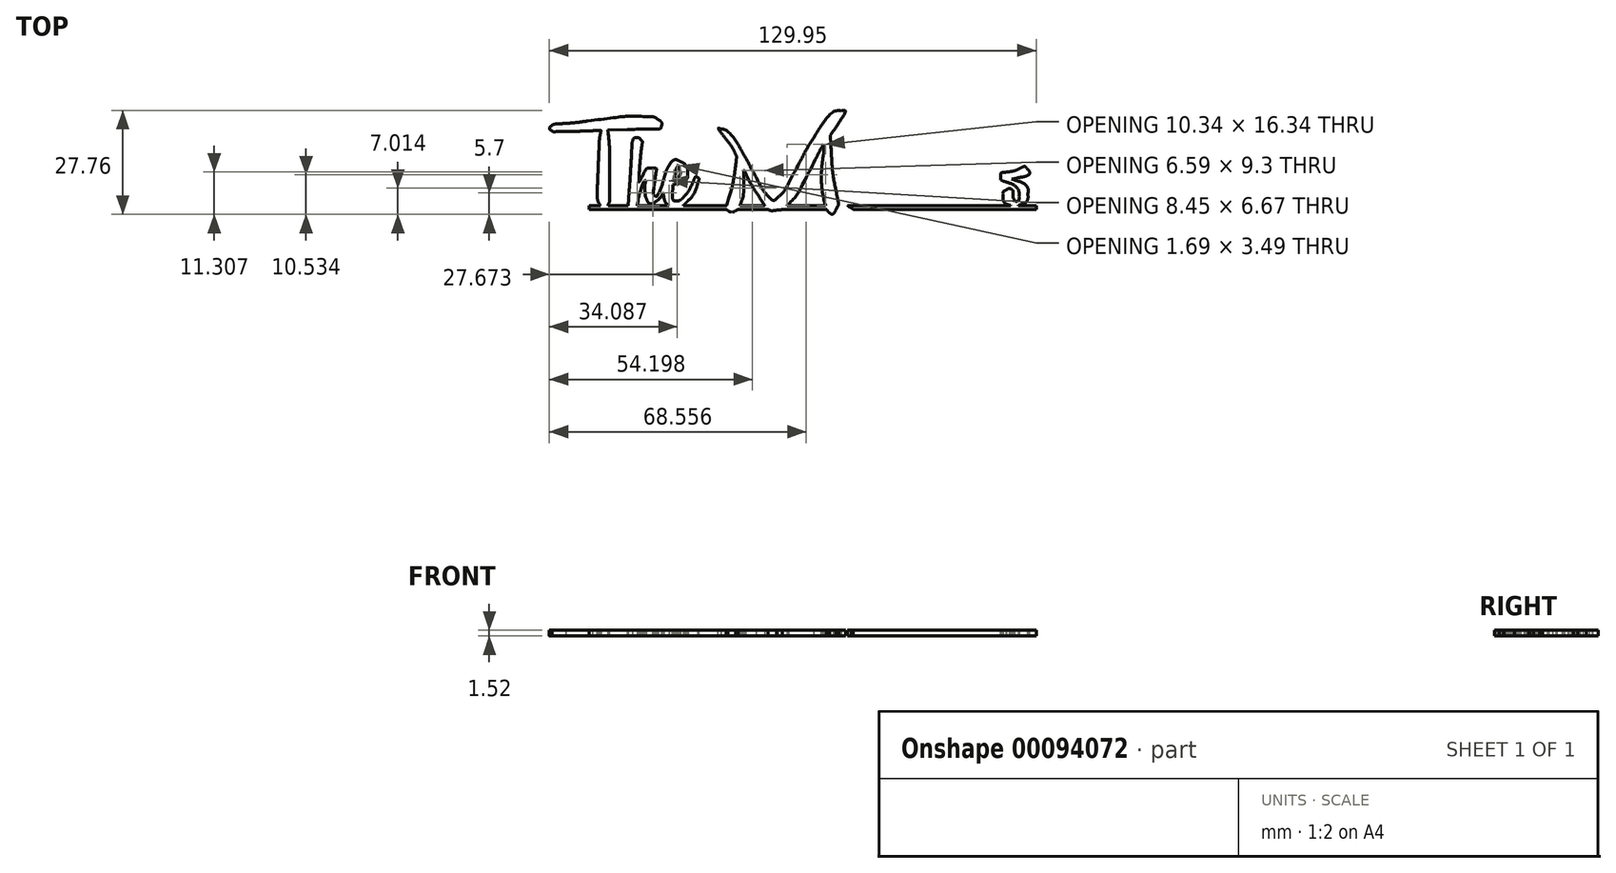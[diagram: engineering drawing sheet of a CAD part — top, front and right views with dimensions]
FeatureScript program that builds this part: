
annotation { "Feature Type Name" : "Feature", "Feature Type Description" : "" }
export const myFeature = defineFeature(function(context is Context, id is Id, definition is map)
    precondition{}
    {
        {
            var Q0;
            Q0=qCreatedBy(makeId("Top.planeOp"),FACE);
            var sketch = newSketch(context, id + "F0", { "sketchPlane" : qUnion([Q0])});
            skLineSegment(sketch, "E0", {"start": v(8.55, 2.32) * mm, "end": v(8.5, 2.84) * mm});
            skLineSegment(sketch, "E1", {"start": v(8.5, 2.84) * mm, "end": v(8.07, 2.18) * mm});
            skLineSegment(sketch, "E2", {"start": v(8.07, 2.18) * mm, "end": v(8.55, 2.32) * mm});
            skLineSegment(sketch, "E3", {"start": v(11.05, 6.37) * mm, "end": v(10.27, 5.29) * mm});
            skLineSegment(sketch, "E4", {"start": v(10.27, 5.29) * mm, "end": v(10.4, 2.62) * mm});
            skLineSegment(sketch, "E5", {"start": v(10.4, 2.62) * mm, "end": v(11.05, 6.37) * mm});
            skLineSegment(sketch, "E6", {"start": v(-44.03, 6.78) * mm, "end": v(-49.15, 6.7) * mm});
            skLineSegment(sketch, "E7", {"start": v(-49.15, 6.7) * mm, "end": v(-49.07, 5.94) * mm});
            skLineSegment(sketch, "E8", {"start": v(-49.07, 5.94) * mm, "end": v(-44.03, 6.78) * mm});
            skLineSegment(sketch, "E9", {"start": v(26.41, -4.76) * mm, "end": v(26.32, -5.42) * mm});
            skLineSegment(sketch, "E10", {"start": v(26.32, -5.42) * mm, "end": v(27.3, -5.33) * mm});
            skLineSegment(sketch, "E11", {"start": v(27.3, -5.33) * mm, "end": v(26.41, -4.76) * mm});
            skLineSegment(sketch, "E12", {"start": v(28.58, -5.48) * mm, "end": v(28.88, -5.73) * mm});
            skLineSegment(sketch, "E13", {"start": v(28.88, -5.73) * mm, "end": v(28.67, -6.78) * mm});
            skLineSegment(sketch, "E14", {"start": v(28.67, -6.78) * mm, "end": v(28.58, -5.48) * mm});
            skLineSegment(sketch, "E15", {"start": v(30.62, -0.91) * mm, "end": v(31.32, -0.91) * mm});
            skLineSegment(sketch, "E16", {"start": v(31.32, -0.91) * mm, "end": v(31.39, -0.12) * mm});
            skLineSegment(sketch, "E17", {"start": v(31.39, -0.12) * mm, "end": v(30.62, -0.91) * mm});
            skLineSegment(sketch, "E18", {"start": v(34.08, 0) * mm, "end": v(34.01, -0.78) * mm});
            skLineSegment(sketch, "E19", {"start": v(34.01, -0.78) * mm, "end": v(34.72, -0.78) * mm});
            skLineSegment(sketch, "E20", {"start": v(34.72, -0.78) * mm, "end": v(34.08, 0) * mm});
            skLineSegment(sketch, "E21", {"start": v(33.6, -11.13) * mm, "end": v(33.73, -11.48) * mm});
            skLineSegment(sketch, "E22", {"start": v(33.73, -11.48) * mm, "end": v(34.04, -11.2) * mm});
            skLineSegment(sketch, "E23", {"start": v(34.04, -11.2) * mm, "end": v(33.6, -11.13) * mm});
            skLineSegment(sketch, "E24", {"start": v(43.61, -8.09) * mm, "end": v(43.62, -8.61) * mm});
            skLineSegment(sketch, "E25", {"start": v(43.62, -8.61) * mm, "end": v(43.8, -8.15) * mm});
            skLineSegment(sketch, "E26", {"start": v(43.8, -8.15) * mm, "end": v(43.61, -8.09) * mm});
            skLineSegment(sketch, "E27", {"start": v(45.2, -8.8) * mm, "end": v(45.1, -7.82) * mm});
            skLineSegment(sketch, "E28", {"start": v(45.1, -7.82) * mm, "end": v(44.76, -8.55) * mm});
            skLineSegment(sketch, "E29", {"start": v(44.76, -8.55) * mm, "end": v(45.2, -8.8) * mm});
            skLineSegment(sketch, "E30", {"start": v(41.23, -11.08) * mm, "end": v(41.23, -10.34) * mm});
            skLineSegment(sketch, "E31", {"start": v(41.23, -10.34) * mm, "end": v(40.72, -11.2) * mm});
            skLineSegment(sketch, "E32", {"start": v(40.72, -11.2) * mm, "end": v(41.23, -11.08) * mm});
            skLineSegment(sketch, "E33", {"start": v(36.47, -11.02) * mm, "end": v(36.31, -10.52) * mm});
            skLineSegment(sketch, "E34", {"start": v(36.31, -10.52) * mm, "end": v(35.94, -11.2) * mm});
            skLineSegment(sketch, "E35", {"start": v(35.94, -11.2) * mm, "end": v(36.47, -11.02) * mm});
            skLineSegment(sketch, "E36", {"start": v(31.17, -11.28) * mm, "end": v(31, -10.46) * mm});
            skLineSegment(sketch, "E37", {"start": v(31, -10.46) * mm, "end": v(30.7, -11.04) * mm});
            skLineSegment(sketch, "E38", {"start": v(30.7, -11.04) * mm, "end": v(31.17, -11.28) * mm});
            skLineSegment(sketch, "E39", {"start": v(20.22, -12.06) * mm, "end": v(19.85, -11.6) * mm});
            skLineSegment(sketch, "E40", {"start": v(19.85, -11.6) * mm, "end": v(19.56, -12.22) * mm});
            skLineSegment(sketch, "E41", {"start": v(19.56, -12.22) * mm, "end": v(20.22, -12.06) * mm});
            skLineSegment(sketch, "E42", {"start": v(17.89, -12.47) * mm, "end": v(17.89, -12.47) * mm});
            skLineSegment(sketch, "E43", {"start": v(-43.45, -13.85) * mm, "end": v(-43.74, -13.61) * mm});
            skLineSegment(sketch, "E44", {"start": v(-43.74, -13.61) * mm, "end": v(-43.47, -9.8) * mm});
            skLineSegment(sketch, "E45", {"start": v(-43.47, -9.8) * mm, "end": v(-43.45, -13.85) * mm});
            skLineSegment(sketch, "E46", {"start": v(-30.74, -7.76) * mm, "end": v(-31.8, -7.97) * mm});
            skLineSegment(sketch, "E47", {"start": v(-31.8, -7.97) * mm, "end": v(-31.83, -9.31) * mm});
            skLineSegment(sketch, "E48", {"start": v(-31.83, -9.31) * mm, "end": v(-30.74, -7.76) * mm});
            skLineSegment(sketch, "E49", {"start": v(59.14, -6.38) * mm, "end": v(58.68, -6.48) * mm});
            skLineSegment(sketch, "E50", {"start": v(58.68, -6.48) * mm, "end": v(59.34, -6.7) * mm});
            skLineSegment(sketch, "E51", {"start": v(59.34, -6.7) * mm, "end": v(59.14, -6.38) * mm});
            skFitSpline(sketch, "E52", {"points": [v(10.05, -15.46) * mm, v(9.66, -15.18) * mm, v(9.18, -14.22) * mm, v(8.91, -13.16) * mm]});
            skFitSpline(sketch, "E53", {"points": [v(8.91, -13.16) * mm, v(8.15, -10.15) * mm, v(7.9, -4.36) * mm, v(8.35, -0.32) * mm]});
            skFitSpline(sketch, "E54", {"points": [v(8.35, -0.32) * mm, v(8.48, 0.84) * mm, v(8.57, 2.03) * mm, v(8.55, 2.32) * mm]});
            skFitSpline(sketch, "E55", {"points": [v(8.07, 2.18) * mm, v(7.84, 1.82) * mm, v(7.2, 0.64) * mm, v(6.64, -0.45) * mm]});
            skFitSpline(sketch, "E56", {"points": [v(6.64, -0.45) * mm, v(2.6, -8.4) * mm, v(0.9, -11.22) * mm, v(-0.92, -13.04) * mm]});
            skFitSpline(sketch, "E57", {"points": [v(-0.92, -13.04) * mm, v(-2.11, -14.22) * mm, v(-2.9, -14.64) * mm, v(-4.04, -14.72) * mm]});
            skFitSpline(sketch, "E58", {"points": [v(-4.04, -14.72) * mm, v(-5.8, -14.83) * mm, v(-7.07, -13.74) * mm, v(-9.5, -10) * mm]});
            skFitSpline(sketch, "E59", {"points": [v(-9.5, -10) * mm, v(-10.49, -8.48) * mm, v(-11.77, -6.2) * mm, v(-12.36, -4.9) * mm]});
            skFitSpline(sketch, "E60", {"points": [v(-12.36, -4.9) * mm, v(-12.54, -4.51) * mm, v(-12.73, -4.2) * mm, v(-12.79, -4.2) * mm]});
            skFitSpline(sketch, "E61", {"points": [v(-12.79, -4.2) * mm, v(-12.85, -4.2) * mm, v(-12.9, -5.31) * mm, v(-12.9, -6.67) * mm]});
            skFitSpline(sketch, "E62", {"points": [v(-12.9, -6.67) * mm, v(-12.9, -9.72) * mm, v(-13.06, -11.2) * mm, v(-13.55, -12.6) * mm]});
            skFitSpline(sketch, "E63", {"points": [v(-13.55, -12.6) * mm, v(-14, -13.93) * mm, v(-14.38, -14.5) * mm, v(-15.05, -14.88) * mm]});
            skFitSpline(sketch, "E64", {"points": [v(-15.05, -14.88) * mm, v(-15.65, -15.21) * mm, v(-16.6, -15.17) * mm, v(-17.19, -14.79) * mm]});
            skFitSpline(sketch, "E65", {"points": [v(-17.19, -14.79) * mm, v(-17.51, -14.57) * mm, v(-17.53, -14.51) * mm, v(-17.46, -13.86) * mm]});
            skFitSpline(sketch, "E66", {"points": [v(-17.46, -13.86) * mm, v(-17.41, -13.48) * mm, v(-17.16, -12.47) * mm, v(-16.9, -11.62) * mm]});
            skFitSpline(sketch, "E67", {"points": [v(-16.9, -11.62) * mm, v(-16.08, -8.9) * mm, v(-15.43, -5.59) * mm, v(-14.9, -1.44) * mm]});
            skFitSpline(sketch, "E68", {"points": [v(-14.9, -1.44) * mm, v(-14.77, -0.47) * mm, v(-14.78, -0.43) * mm, v(-15.2, 0.5) * mm]});
            skFitSpline(sketch, "E69", {"points": [v(-15.2, 0.5) * mm, v(-15.7, 1.58) * mm, v(-16.3, 2.49) * mm, v(-17.9, 4.62) * mm]});
            skFitSpline(sketch, "E70", {"points": [v(-17.9, 4.62) * mm, v(-19.5, 6.73) * mm, v(-19.66, 7.1) * mm, v(-18.99, 6.93) * mm]});
            skFitSpline(sketch, "E71", {"points": [v(-18.99, 6.93) * mm, v(-17.63, 6.6) * mm, v(-15.05, 3.84) * mm, v(-13.26, 0.78) * mm]});
            skFitSpline(sketch, "E72", {"points": [v(-13.26, 0.78) * mm, v(-12.86, 0.1) * mm, v(-11.8, -1.81) * mm, v(-10.93, -3.47) * mm]});
            skFitSpline(sketch, "E73", {"points": [v(-10.93, -3.47) * mm, v(-8.28, -8.46) * mm, v(-7.49, -9.76) * mm, v(-6.46, -10.83) * mm]});
            skFitSpline(sketch, "E74", {"points": [v(-6.46, -10.83) * mm, v(-5.31, -12.03) * mm, v(-4.66, -12.14) * mm, v(-3.74, -11.3) * mm]});
            skFitSpline(sketch, "E75", {"points": [v(-3.74, -11.3) * mm, v(-2.47, -10.12) * mm, v(-1.25, -8.2) * mm, v(1.55, -2.9) * mm]});
            skFitSpline(sketch, "E76", {"points": [v(1.55, -2.9) * mm, v(3.65, 1.06) * mm, v(4.61, 2.76) * mm, v(5.77, 4.55) * mm]});
            skFitSpline(sketch, "E77", {"points": [v(5.77, 4.55) * mm, v(8.66, 9) * mm, v(11.34, 11.64) * mm, v(13.12, 11.76) * mm]});
            skFitSpline(sketch, "E78", {"points": [v(13.12, 11.76) * mm, v(14.2, 11.83) * mm, v(14.08, 11.11) * mm, v(12.57, 8.66) * mm]});
            skFitSpline(sketch, "E79", {"points": [v(12.57, 8.66) * mm, v(12.16, 8) * mm, v(11.47, 6.96) * mm, v(11.05, 6.37) * mm]});
            skFitSpline(sketch, "E80", {"points": [v(10.4, 2.62) * mm, v(10.68, -2.42) * mm, v(11.06, -6.05) * mm, v(11.6, -8.81) * mm]});
            skFitSpline(sketch, "E81", {"points": [v(11.6, -8.81) * mm, v(12.35, -12.63) * mm, v(12.38, -13.33) * mm, v(11.8, -14.47) * mm]});
            skFitSpline(sketch, "E82", {"points": [v(11.8, -14.47) * mm, v(11.28, -15.49) * mm, v(10.62, -15.86) * mm, v(10.05, -15.46) * mm]});
            skFitSpline(sketch, "E83", {"points": [v(-50.1, -14.15) * mm, v(-50.65, -13.91) * mm, v(-51.56, -12.92) * mm, v(-51.73, -12.37) * mm]});
            skFitSpline(sketch, "E84", {"points": [v(-51.73, -12.37) * mm, v(-51.95, -11.68) * mm, v(-51.97, -9.22) * mm, v(-51.78, -4.66) * mm]});
            skFitSpline(sketch, "E85", {"points": [v(-51.78, -4.66) * mm, v(-51.49, 2.35) * mm, v(-51.36, 4.44) * mm, v(-51.16, 5.5) * mm]});
            skFitSpline(sketch, "E86", {"points": [v(-51.16, 5.5) * mm, v(-51.05, 6.05) * mm, v(-50.98, 6.52) * mm, v(-51, 6.53) * mm]});
            skFitSpline(sketch, "E87", {"points": [v(-51, 6.53) * mm, v(-51.01, 6.54) * mm, v(-52.03, 6.5) * mm, v(-53.26, 6.45) * mm]});
            skFitSpline(sketch, "E88", {"points": [v(-53.26, 6.45) * mm, v(-54.5, 6.4) * mm, v(-57.34, 6.31) * mm, v(-59.58, 6.26) * mm]});
            skFitSpline(sketch, "E89", {"points": [v(-59.58, 6.26) * mm, v(-63.56, 6.18) * mm, v(-63.68, 6.19) * mm, v(-64.1, 6.45) * mm]});
            skFitSpline(sketch, "E90", {"points": [v(-64.1, 6.45) * mm, v(-64.65, 6.8) * mm, v(-64.68, 7.37) * mm, v(-64.19, 7.76) * mm]});
            skFitSpline(sketch, "E91", {"points": [v(-64.19, 7.76) * mm, v(-63.74, 8.11) * mm, v(-62.93, 8.25) * mm, v(-60.3, 8.42) * mm]});
            skFitSpline(sketch, "E92", {"points": [v(-60.3, 8.42) * mm, v(-59.11, 8.5) * mm, v(-56.5, 8.77) * mm, v(-54.51, 9.03) * mm]});
            skFitSpline(sketch, "E93", {"points": [v(-54.51, 9.03) * mm, v(-46.34, 10.09) * mm, v(-43.17, 10.35) * mm, v(-39.68, 10.25) * mm]});
            skFitSpline(sketch, "E94", {"points": [v(-39.68, 10.25) * mm, v(-37.3, 10.19) * mm, v(-36.64, 10.05) * mm, v(-35.67, 9.4) * mm]});
            skFitSpline(sketch, "E95", {"points": [v(-35.67, 9.4) * mm, v(-35.05, 9) * mm, v(-34.68, 8.27) * mm, v(-34.84, 7.8) * mm]});
            skFitSpline(sketch, "E96", {"points": [v(-34.84, 7.8) * mm, v(-35.1, 7.06) * mm, v(-36.56, 6.9) * mm, v(-44.03, 6.78) * mm]});
            skFitSpline(sketch, "E97", {"points": [v(-49.07, 5.94) * mm, v(-48.78, 3.12) * mm, v(-48.66, 0.18) * mm, v(-48.66, -5) * mm]});
            skFitSpline(sketch, "E98", {"points": [v(-48.66, -5) * mm, v(-48.65, -11) * mm, v(-48.75, -12.57) * mm, v(-49.2, -13.69) * mm]});
            skFitSpline(sketch, "E99", {"points": [v(-49.2, -13.69) * mm, v(-49.44, -14.3) * mm, v(-49.6, -14.37) * mm, v(-50.1, -14.15) * mm]});
            skFitSpline(sketch, "E100", {"points": [v(15.79, -14.07) * mm, v(14.9, -13.6) * mm, v(14.27, -12.5) * mm, v(13.9, -10.73) * mm]});
            skFitSpline(sketch, "E101", {"points": [v(13.9, -10.73) * mm, v(13.65, -9.5) * mm, v(13.65, -8.88) * mm, v(13.9, -7.43) * mm]});
            skFitSpline(sketch, "E102", {"points": [v(13.9, -7.43) * mm, v(14.27, -5.37) * mm, v(15.27, -3.7) * mm, v(16.5, -3.11) * mm]});
            skFitSpline(sketch, "E103", {"points": [v(16.5, -3.11) * mm, v(17.07, -2.84) * mm, v(18.16, -2.82) * mm, v(18.76, -3.07) * mm]});
            skFitSpline(sketch, "E104", {"points": [v(18.76, -3.07) * mm, v(19, -3.17) * mm, v(19.37, -3.46) * mm, v(19.57, -3.71) * mm]});
            skFitSpline(sketch, "E105", {"points": [v(19.57, -3.71) * mm, v(19.92, -4.15) * mm, v(19.95, -4.16) * mm, v(20.28, -3.97) * mm]});
            skFitSpline(sketch, "E106", {"points": [v(20.28, -3.97) * mm, v(20.74, -3.7) * mm, v(21.53, -3.85) * mm, v(21.95, -4.27) * mm]});
            skFitSpline(sketch, "E107", {"points": [v(21.95, -4.27) * mm, v(22.3, -4.62) * mm, v(22.36, -5.33) * mm, v(22.14, -6.44) * mm]});
            skFitSpline(sketch, "E108", {"points": [v(22.14, -6.44) * mm, v(22.07, -6.77) * mm, v(21.98, -7.69) * mm, v(21.93, -8.48) * mm]});
            skFitSpline(sketch, "E109", {"points": [v(21.93, -8.48) * mm, v(21.83, -10.14) * mm, v(22, -11.1) * mm, v(22.37, -11.03) * mm]});
            skFitSpline(sketch, "E110", {"points": [v(22.37, -11.03) * mm, v(22.7, -10.96) * mm, v(23.38, -9.6) * mm, v(23.99, -7.74) * mm]});
            skFitSpline(sketch, "E111", {"points": [v(23.99, -7.74) * mm, v(24.42, -6.4) * mm, v(24.5, -6.02) * mm, v(24.39, -5.8) * mm]});
            skFitSpline(sketch, "E112", {"points": [v(24.39, -5.8) * mm, v(24.3, -5.66) * mm, v(24.24, -5.3) * mm, v(24.24, -4.99) * mm]});
            skFitSpline(sketch, "E113", {"points": [v(24.24, -4.99) * mm, v(24.24, -4.54) * mm, v(24.32, -4.36) * mm, v(24.69, -4) * mm]});
            skFitSpline(sketch, "E114", {"points": [v(24.69, -4) * mm, v(25.05, -3.63) * mm, v(25.24, -3.54) * mm, v(25.67, -3.54) * mm]});
            skFitSpline(sketch, "E115", {"points": [v(25.67, -3.54) * mm, v(26.36, -3.54) * mm, v(26.54, -3.84) * mm, v(26.41, -4.76) * mm]});
            skFitSpline(sketch, "E116", {"points": [v(27.3, -5.33) * mm, v(28.14, -5.25) * mm, v(28.31, -5.27) * mm, v(28.58, -5.48) * mm]});
            skFitSpline(sketch, "E117", {"points": [v(28.67, -6.78) * mm, v(28.05, -9.98) * mm, v(28.04, -11.58) * mm, v(28.65, -11.58) * mm]});
            skFitSpline(sketch, "E118", {"points": [v(28.65, -11.58) * mm, v(28.93, -11.58) * mm, v(29.43, -10.65) * mm, v(30.19, -8.75) * mm]});
            skFitSpline(sketch, "E119", {"points": [v(30.19, -8.75) * mm, v(30.83, -7.12) * mm, v(30.87, -6.93) * mm, v(31.04, -5.06) * mm]});
            skFitSpline(sketch, "E120", {"points": [v(31.04, -5.06) * mm, v(31.3, -2.01) * mm, v(31.34, -2.23) * mm, v(30.57, -2.23) * mm]});
            skFitSpline(sketch, "E121", {"points": [v(30.57, -2.23) * mm, v(29.55, -2.23) * mm, v(29, -1.88) * mm, v(29.2, -1.36) * mm]});
            skFitSpline(sketch, "E122", {"points": [v(29.2, -1.36) * mm, v(29.31, -1.07) * mm, v(29.8, -0.91) * mm, v(30.62, -0.91) * mm]});
            skFitSpline(sketch, "E123", {"points": [v(31.39, -0.12) * mm, v(31.43, 0.32) * mm, v(31.55, 0.82) * mm, v(31.67, 1) * mm]});
            skFitSpline(sketch, "E124", {"points": [v(31.67, 1) * mm, v(31.96, 1.45) * mm, v(32.8, 1.65) * mm, v(33.36, 1.42) * mm]});
            skFitSpline(sketch, "E125", {"points": [v(33.36, 1.42) * mm, v(34.05, 1.13) * mm, v(34.16, 0.9) * mm, v(34.08, 0) * mm]});
            skFitSpline(sketch, "E126", {"points": [v(34.72, -0.78) * mm, v(35.4, -0.78) * mm, v(35.44, -0.76) * mm, v(35.62, -0.34) * mm]});
            skFitSpline(sketch, "E127", {"points": [v(35.62, -0.34) * mm, v(36.27, 1.24) * mm, v(39.63, 1.57) * mm, v(40.38, 0.14) * mm]});
            skFitSpline(sketch, "E128", {"points": [v(40.38, 0.14) * mm, v(41.17, -1.39) * mm, v(38.77, -2.85) * mm, v(36.6, -2.17) * mm]});
            skFitSpline(sketch, "E129", {"points": [v(36.6, -2.17) * mm, v(36.05, -2) * mm, v(35.8, -1.98) * mm, v(35.52, -2.09) * mm]});
            skFitSpline(sketch, "E130", {"points": [v(35.52, -2.09) * mm, v(35.32, -2.16) * mm, v(34.87, -2.23) * mm, v(34.51, -2.23) * mm]});
            skFitSpline(sketch, "E131", {"points": [v(34.51, -2.23) * mm, v(33.89, -2.23) * mm, v(33.86, -2.24) * mm, v(33.8, -2.66) * mm]});
            skFitSpline(sketch, "E132", {"points": [v(33.8, -2.66) * mm, v(33.49, -4.52) * mm, v(33.35, -10.47) * mm, v(33.6, -11.13) * mm]});
            skFitSpline(sketch, "E133", {"points": [v(34.04, -11.2) * mm, v(34.39, -10.87) * mm, v(35.33, -9.03) * mm, v(35.95, -7.47) * mm]});
            skFitSpline(sketch, "E134", {"points": [v(35.95, -7.47) * mm, v(36.24, -6.77) * mm, v(36.36, -6.24) * mm, v(36.36, -5.72) * mm]});
            skFitSpline(sketch, "E135", {"points": [v(36.36, -5.72) * mm, v(36.36, -4.24) * mm, v(37.02, -3.56) * mm, v(38.1, -3.95) * mm]});
            skFitSpline(sketch, "E136", {"points": [v(38.1, -3.95) * mm, v(38.4, -4.05) * mm, v(38.75, -4.3) * mm, v(38.9, -4.48) * mm]});
            skFitSpline(sketch, "E137", {"points": [v(38.9, -4.48) * mm, v(39.14, -4.82) * mm, v(39.14, -4.86) * mm, v(38.93, -6.13) * mm]});
            skFitSpline(sketch, "E138", {"points": [v(38.93, -6.13) * mm, v(38.69, -7.53) * mm, v(38.6, -10.1) * mm, v(38.77, -10.7) * mm]});
            skFitSpline(sketch, "E139", {"points": [v(38.77, -10.7) * mm, v(38.9, -11.18) * mm, v(39.22, -11.12) * mm, v(39.6, -10.56) * mm]});
            skFitSpline(sketch, "E140", {"points": [v(39.6, -10.56) * mm, v(40.16, -9.72) * mm, v(40.98, -7.2) * mm, v(41.16, -5.73) * mm]});
            skFitSpline(sketch, "E141", {"points": [v(41.16, -5.73) * mm, v(41.26, -4.93) * mm, v(41.42, -4.2) * mm, v(41.54, -4) * mm]});
            skFitSpline(sketch, "E142", {"points": [v(41.54, -4) * mm, v(41.95, -3.4) * mm, v(42.93, -3.1) * mm, v(43.73, -3.34) * mm]});
            skFitSpline(sketch, "E143", {"points": [v(43.73, -3.34) * mm, v(44.22, -3.5) * mm, v(44.25, -3.9) * mm, v(43.92, -5.78) * mm]});
            skFitSpline(sketch, "E144", {"points": [v(43.92, -5.78) * mm, v(43.75, -6.76) * mm, v(43.61, -7.8) * mm, v(43.61, -8.09) * mm]});
            skFitSpline(sketch, "E145", {"points": [v(43.8, -8.15) * mm, v(44.06, -7.42) * mm, v(44.65, -6.29) * mm, v(45.02, -5.8) * mm]});
            skFitSpline(sketch, "E146", {"points": [v(45.02, -5.8) * mm, v(45.6, -5.03) * mm, v(46.93, -4.73) * mm, v(47.55, -5.23) * mm]});
            skFitSpline(sketch, "E147", {"points": [v(47.55, -5.23) * mm, v(47.82, -5.45) * mm, v(47.83, -5.5) * mm, v(47.67, -6.05) * mm]});
            skFitSpline(sketch, "E148", {"points": [v(47.67, -6.05) * mm, v(47.46, -6.78) * mm, v(47.43, -9.8) * mm, v(47.63, -10) * mm]});
            skFitSpline(sketch, "E149", {"points": [v(47.63, -10) * mm, v(48, -10.37) * mm, v(48.82, -9.38) * mm, v(49.86, -7.3) * mm]});
            skFitSpline(sketch, "E150", {"points": [v(49.86, -7.3) * mm, v(50.52, -5.97) * mm, v(50.78, -5.72) * mm, v(51.18, -6.05) * mm]});
            skFitSpline(sketch, "E151", {"points": [v(51.18, -6.05) * mm, v(51.54, -6.35) * mm, v(51.4, -7.04) * mm, v(50.65, -8.51) * mm]});
            skFitSpline(sketch, "E152", {"points": [v(50.65, -8.51) * mm, v(49.8, -10.21) * mm, v(48.62, -11.62) * mm, v(47.83, -11.85) * mm]});
            skFitSpline(sketch, "E153", {"points": [v(47.83, -11.85) * mm, v(47.06, -12.08) * mm, v(46.32, -11.82) * mm, v(45.84, -11.16) * mm]});
            skFitSpline(sketch, "E154", {"points": [v(45.84, -11.16) * mm, v(45.42, -10.59) * mm, v(45.34, -10.29) * mm, v(45.2, -8.8) * mm]});
            skFitSpline(sketch, "E155", {"points": [v(44.76, -8.55) * mm, v(44.58, -8.95) * mm, v(44.33, -9.72) * mm, v(44.2, -10.26) * mm]});
            skFitSpline(sketch, "E156", {"points": [v(44.2, -10.26) * mm, v(43.78, -12.15) * mm, v(43.76, -12.2) * mm, v(43.28, -12.42) * mm]});
            skFitSpline(sketch, "E157", {"points": [v(43.28, -12.42) * mm, v(42.73, -12.68) * mm, v(42.25, -12.69) * mm, v(41.77, -12.44) * mm]});
            skFitSpline(sketch, "E158", {"points": [v(41.77, -12.44) * mm, v(41.3, -12.2) * mm, v(41.23, -12.01) * mm, v(41.23, -11.08) * mm]});
            skFitSpline(sketch, "E159", {"points": [v(40.72, -11.2) * mm, v(40.1, -12.23) * mm, v(39.29, -12.9) * mm, v(38.65, -12.9) * mm]});
            skFitSpline(sketch, "E160", {"points": [v(38.65, -12.9) * mm, v(37.65, -12.9) * mm, v(36.82, -12.18) * mm, v(36.47, -11.02) * mm]});
            skFitSpline(sketch, "E161", {"points": [v(35.94, -11.2) * mm, v(35.1, -12.72) * mm, v(34.12, -13.55) * mm, v(33.13, -13.55) * mm]});
            skFitSpline(sketch, "E162", {"points": [v(33.13, -13.55) * mm, v(32.11, -13.55) * mm, v(31.48, -12.82) * mm, v(31.17, -11.28) * mm]});
            skFitSpline(sketch, "E163", {"points": [v(30.7, -11.04) * mm, v(30.31, -11.8) * mm, v(29.3, -12.89) * mm, v(28.76, -13.11) * mm]});
            skFitSpline(sketch, "E164", {"points": [v(28.76, -13.11) * mm, v(28.12, -13.38) * mm, v(27.24, -13.34) * mm, v(26.84, -13.02) * mm]});
            skFitSpline(sketch, "E165", {"points": [v(26.84, -13.02) * mm, v(26.65, -12.88) * mm, v(26.37, -12.42) * mm, v(26.2, -12) * mm]});
            skFitSpline(sketch, "E166", {"points": [v(26.2, -12) * mm, v(25.84, -11.05) * mm, v(25.8, -8.95) * mm, v(26.13, -7.59) * mm]});
            skFitSpline(sketch, "E167", {"points": [v(26.13, -7.59) * mm, v(26.4, -6.45) * mm, v(26.4, -6.47) * mm, v(26.04, -6.54) * mm]});
            skFitSpline(sketch, "E168", {"points": [v(26.04, -6.54) * mm, v(25.77, -6.59) * mm, v(25.68, -6.76) * mm, v(25.43, -7.6) * mm]});
            skFitSpline(sketch, "E169", {"points": [v(25.43, -7.6) * mm, v(24.7, -10.16) * mm, v(23.79, -11.88) * mm, v(22.84, -12.53) * mm]});
            skFitSpline(sketch, "E170", {"points": [v(22.84, -12.53) * mm, v(21.97, -13.13) * mm, v(20.92, -12.94) * mm, v(20.22, -12.06) * mm]});
            skFitSpline(sketch, "E171", {"points": [v(19.56, -12.22) * mm, v(18.74, -13.99) * mm, v(17.13, -14.78) * mm, v(15.79, -14.07) * mm]});
            skFitSpline(sketch, "E172", {"points": [v(17.89, -12.47) * mm, v(18.3, -12.03) * mm, v(18.78, -10.98) * mm, v(19.05, -9.93) * mm]});
            skFitSpline(sketch, "E173", {"points": [v(19.05, -9.93) * mm, v(19.39, -8.66) * mm, v(19.4, -6.35) * mm, v(19.06, -5.5) * mm]});
            skFitSpline(sketch, "E174", {"points": [v(19.06, -5.5) * mm, v(18.51, -4.06) * mm, v(17.25, -4.74) * mm, v(16.59, -6.83) * mm]});
            skFitSpline(sketch, "E175", {"points": [v(16.59, -6.83) * mm, v(16.4, -7.42) * mm, v(16.29, -8.2) * mm, v(16.24, -9.3) * mm]});
            skFitSpline(sketch, "E176", {"points": [v(16.24, -9.3) * mm, v(16.14, -11.61) * mm, v(16.47, -12.76) * mm, v(17.24, -12.76) * mm]});
            skFitSpline(sketch, "E177", {"points": [v(17.24, -12.76) * mm, v(17.45, -12.76) * mm, v(17.73, -12.64) * mm, v(17.89, -12.47) * mm]});
            skFitSpline(sketch, "E178", {"points": [v(-43.47, -9.8) * mm, v(-43.15, -5.38) * mm, v(-42.97, -2.49) * mm, v(-42.8, 0.94) * mm]});
            skFitSpline(sketch, "E179", {"points": [v(-42.8, 0.94) * mm, v(-42.73, 2.28) * mm, v(-42.61, 3.54) * mm, v(-42.52, 3.72) * mm]});
            skFitSpline(sketch, "E180", {"points": [v(-42.52, 3.72) * mm, v(-42.19, 4.47) * mm, v(-40.97, 4.6) * mm, v(-40.3, 3.96) * mm]});
            skFitSpline(sketch, "E181", {"points": [v(-40.3, 3.96) * mm, v(-39.93, 3.63) * mm, v(-39.88, 3.5) * mm, v(-39.94, 3.14) * mm]});
            skFitSpline(sketch, "E182", {"points": [v(-39.94, 3.14) * mm, v(-40.14, 2.08) * mm, v(-40.82, -5.73) * mm, v(-40.81, -6.84) * mm]});
            skFitSpline(sketch, "E183", {"points": [v(-40.81, -6.84) * mm, v(-40.81, -7.27) * mm, v(-40.78, -7.23) * mm, v(-40.23, -6.22) * mm]});
            skFitSpline(sketch, "E184", {"points": [v(-40.23, -6.22) * mm, v(-39.04, -4) * mm, v(-38.53, -3.54) * mm, v(-37.22, -3.54) * mm]});
            skFitSpline(sketch, "E185", {"points": [v(-37.22, -3.54) * mm, v(-36.38, -3.54) * mm, v(-36.15, -3.77) * mm, v(-36.26, -4.48) * mm]});
            skFitSpline(sketch, "E186", {"points": [v(-36.26, -4.48) * mm, v(-36.72, -7.57) * mm, v(-36.9, -10.67) * mm, v(-36.62, -10.85) * mm]});
            skFitSpline(sketch, "E187", {"points": [v(-36.62, -10.85) * mm, v(-36.23, -11.09) * mm, v(-34.84, -8.47) * mm, v(-34.17, -6.22) * mm]});
            skFitSpline(sketch, "E188", {"points": [v(-34.17, -6.22) * mm, v(-33.6, -4.32) * mm, v(-33.4, -3.81) * mm, v(-32.8, -2.91) * mm]});
            skFitSpline(sketch, "E189", {"points": [v(-32.8, -2.91) * mm, v(-32, -1.66) * mm, v(-30.92, -1.25) * mm, v(-29.8, -1.78) * mm]});
            skFitSpline(sketch, "E190", {"points": [v(-29.8, -1.78) * mm, v(-28.75, -2.28) * mm, v(-27.9, -3.83) * mm, v(-27.86, -5.28) * mm]});
            skFitSpline(sketch, "E191", {"points": [v(-27.86, -5.28) * mm, v(-27.85, -6.09) * mm, v(-27.88, -6.2) * mm, v(-28.24, -6.58) * mm]});
            skFitSpline(sketch, "E192", {"points": [v(-28.24, -6.58) * mm, v(-28.8, -7.17) * mm, v(-29.54, -7.52) * mm, v(-30.74, -7.76) * mm]});
            skFitSpline(sketch, "E193", {"points": [v(-31.83, -9.31) * mm, v(-31.9, -11.4) * mm, v(-31.55, -12.24) * mm, v(-30.63, -12.24) * mm]});
            skFitSpline(sketch, "E194", {"points": [v(-30.63, -12.24) * mm, v(-30.15, -12.24) * mm, v(-29.46, -11.8) * mm, v(-28.74, -11.03) * mm]});
            skFitSpline(sketch, "E195", {"points": [v(-28.74, -11.03) * mm, v(-28.14, -10.39) * mm, v(-27, -8.5) * mm, v(-26.4, -7.2) * mm]});
            skFitSpline(sketch, "E196", {"points": [v(-26.4, -7.2) * mm, v(-25.88, -6.01) * mm, v(-25.63, -5.79) * mm, v(-25.15, -6.04) * mm]});
            skFitSpline(sketch, "E197", {"points": [v(-25.15, -6.04) * mm, v(-24.8, -6.23) * mm, v(-24.81, -6.58) * mm, v(-25.22, -7.83) * mm]});
            skFitSpline(sketch, "E198", {"points": [v(-25.22, -7.83) * mm, v(-25.8, -9.63) * mm, v(-26.67, -11.14) * mm, v(-27.7, -12.18) * mm]});
            skFitSpline(sketch, "E199", {"points": [v(-27.7, -12.18) * mm, v(-28.94, -13.42) * mm, v(-29.87, -13.88) * mm, v(-31.13, -13.87) * mm]});
            skFitSpline(sketch, "E200", {"points": [v(-31.13, -13.87) * mm, v(-31.72, -13.87) * mm, v(-32.2, -13.8) * mm, v(-32.45, -13.66) * mm]});
            skFitSpline(sketch, "E201", {"points": [v(-32.45, -13.66) * mm, v(-33.3, -13.2) * mm, v(-33.98, -12.16) * mm, v(-34.25, -10.9) * mm]});
            skFitSpline(sketch, "E202", {"points": [v(-34.25, -10.9) * mm, v(-34.38, -10.29) * mm, v(-34.42, -10.23) * mm, v(-34.55, -10.45) * mm]});
            skFitSpline(sketch, "E203", {"points": [v(-34.55, -10.45) * mm, v(-34.87, -11) * mm, v(-35.79, -12.06) * mm, v(-36.18, -12.32) * mm]});
            skFitSpline(sketch, "E204", {"points": [v(-36.18, -12.32) * mm, v(-37.24, -13.03) * mm, v(-38.28, -12.77) * mm, v(-38.84, -11.64) * mm]});
            skFitSpline(sketch, "E205", {"points": [v(-38.84, -11.64) * mm, v(-39.12, -11.09) * mm, v(-39.18, -10.76) * mm, v(-39.22, -9.52) * mm]});
            skFitSpline(sketch, "E206", {"points": [v(-39.22, -9.52) * mm, v(-39.24, -8.71) * mm, v(-39.2, -7.78) * mm, v(-39.14, -7.44) * mm]});
            skFitSpline(sketch, "E207", {"points": [v(-39.14, -7.44) * mm, v(-39.06, -7.1) * mm, v(-39.03, -6.84) * mm, v(-39.05, -6.84) * mm]});
            skFitSpline(sketch, "E208", {"points": [v(-39.05, -6.84) * mm, v(-39.3, -6.84) * mm, v(-40.85, -10.97) * mm, v(-41.09, -12.25) * mm]});
            skFitSpline(sketch, "E209", {"points": [v(-41.09, -12.25) * mm, v(-41.17, -12.71) * mm, v(-41.26, -13.22) * mm, v(-41.3, -13.39) * mm]});
            skFitSpline(sketch, "E210", {"points": [v(-41.3, -13.39) * mm, v(-41.4, -14.01) * mm, v(-42.86, -14.32) * mm, v(-43.45, -13.85) * mm]});
            skFitSpline(sketch, "E211", {"points": [v(-30.23, -5.79) * mm, v(-29.92, -5.48) * mm, v(-29.82, -4.56) * mm, v(-30, -3.84) * mm]});
            skFitSpline(sketch, "E212", {"points": [v(-30, -3.84) * mm, v(-30.29, -2.8) * mm, v(-30.7, -3.22) * mm, v(-31.2, -5) * mm]});
            skFitSpline(sketch, "E213", {"points": [v(-31.2, -5) * mm, v(-31.35, -5.54) * mm, v(-31.47, -6.03) * mm, v(-31.47, -6.1) * mm]});
            skFitSpline(sketch, "E214", {"points": [v(-31.47, -6.1) * mm, v(-31.47, -6.28) * mm, v(-30.5, -6.05) * mm, v(-30.23, -5.79) * mm]});
            skFitSpline(sketch, "E215", {"points": [v(58.04, -13.36) * mm, v(57.06, -13.01) * mm, v(56.39, -12.05) * mm, v(56.34, -10.93) * mm]});
            skFitSpline(sketch, "E216", {"points": [v(56.34, -10.93) * mm, v(56.3, -10.14) * mm, v(56.53, -9.71) * mm, v(57.16, -9.36) * mm]});
            skFitSpline(sketch, "E217", {"points": [v(57.16, -9.36) * mm, v(57.75, -9.02) * mm, v(58.31, -9) * mm, v(58.72, -9.28) * mm]});
            skFitSpline(sketch, "E218", {"points": [v(58.72, -9.28) * mm, v(58.97, -9.46) * mm, v(59, -9.6) * mm, v(59, -10.45) * mm]});
            skFitSpline(sketch, "E219", {"points": [v(59, -10.45) * mm, v(59, -11.22) * mm, v(59.06, -11.48) * mm, v(59.28, -11.76) * mm]});
            skFitSpline(sketch, "E220", {"points": [v(59.28, -11.76) * mm, v(59.8, -12.42) * mm, v(60.6, -12) * mm, v(60.58, -11.08) * mm]});
            skFitSpline(sketch, "E221", {"points": [v(60.58, -11.08) * mm, v(60.55, -9.51) * mm, v(59.21, -8.04) * mm, v(57.08, -7.21) * mm]});
            skFitSpline(sketch, "E222", {"points": [v(57.08, -7.21) * mm, v(55.92, -6.77) * mm, v(55.72, -6.54) * mm, v(55.72, -5.73) * mm]});
            skFitSpline(sketch, "E223", {"points": [v(55.72, -5.73) * mm, v(55.72, -4.97) * mm, v(56.04, -4.73) * mm, v(57.23, -4.58) * mm]});
            skFitSpline(sketch, "E224", {"points": [v(57.23, -4.58) * mm, v(58.7, -4.4) * mm, v(59.65, -4.15) * mm, v(60.83, -3.6) * mm]});
            skFitSpline(sketch, "E225", {"points": [v(60.83, -3.6) * mm, v(62, -3.07) * mm, v(62.23, -3.08) * mm, v(62.81, -3.75) * mm]});
            skFitSpline(sketch, "E226", {"points": [v(62.81, -3.75) * mm, v(63.34, -4.34) * mm, v(63.4, -5.14) * mm, v(62.93, -5.44) * mm]});
            skFitSpline(sketch, "E227", {"points": [v(62.93, -5.44) * mm, v(62.68, -5.6) * mm, v(61.45, -5.9) * mm, v(59.14, -6.38) * mm]});
            skFitSpline(sketch, "E228", {"points": [v(59.34, -6.7) * mm, v(61.75, -7.53) * mm, v(62.96, -8.78) * mm, v(62.96, -10.46) * mm]});
            skFitSpline(sketch, "E229", {"points": [v(62.96, -10.46) * mm, v(62.96, -11.85) * mm, v(62.2, -12.83) * mm, v(60.7, -13.36) * mm]});
            skFitSpline(sketch, "E230", {"points": [v(60.7, -13.36) * mm, v(60.03, -13.6) * mm, v(58.71, -13.6) * mm, v(58.04, -13.36) * mm]});
            skFitSpline(sketch, "E231", {"points": [v(50.5, -2.42) * mm, v(50.45, -2.31) * mm, v(50.52, -1.82) * mm, v(50.64, -1.34) * mm]});
            skFitSpline(sketch, "E232", {"points": [v(50.64, -1.34) * mm, v(50.98, 0) * mm, v(51.04, 1.96) * mm, v(50.8, 3.43) * mm]});
            skFitSpline(sketch, "E233", {"points": [v(50.8, 3.43) * mm, v(50.67, 4.23) * mm, v(50.64, 4.73) * mm, v(50.72, 4.81) * mm]});
            skFitSpline(sketch, "E234", {"points": [v(50.72, 4.81) * mm, v(50.95, 5.05) * mm, v(51.95, 4.87) * mm, v(52.73, 4.46) * mm]});
            skFitSpline(sketch, "E235", {"points": [v(52.73, 4.46) * mm, v(54.26, 3.64) * mm, v(54.5, 2.8) * mm, v(53.75, 0.85) * mm]});
            skFitSpline(sketch, "E236", {"points": [v(53.75, 0.85) * mm, v(53, -1.12) * mm, v(51.79, -2.62) * mm, v(50.97, -2.62) * mm]});
            skFitSpline(sketch, "E237", {"points": [v(50.97, -2.62) * mm, v(50.74, -2.62) * mm, v(50.54, -2.54) * mm, v(50.5, -2.42) * mm]});
            skLineSegment(sketch, "E238.bottom", {"start": v(-54.17, -13.5) * mm, "end": v(65.2, -13.5) * mm});
            skLineSegment(sketch, "E238.top", {"start": v(-54.17, -14.51) * mm, "end": v(65.2, -14.51) * mm});
            skLineSegment(sketch, "E238.left", {"start": v(-54.17, -13.5) * mm, "end": v(-54.17, -14.51) * mm});
            skLineSegment(sketch, "E238.right", {"start": v(65.2, -13.5) * mm, "end": v(65.2, -14.51) * mm});
            skPoint(sketch, "E239", {"position": v(5.52, -14.51) * mm});
            skLineSegment(sketch, "E240.bottom", {"start": v(8.06, -14.51) * mm, "end": v(2.98, -14.51) * mm});
            skLineSegment(sketch, "E240.top", {"start": v(8.06, -65.31) * mm, "end": v(2.98, -65.31) * mm});
            skLineSegment(sketch, "E240.left", {"start": v(8.06, -14.51) * mm, "end": v(8.06, -65.31) * mm});
            skLineSegment(sketch, "E240.right", {"start": v(2.98, -14.51) * mm, "end": v(2.98, -65.31) * mm});
            skSolve(sketch);
        }
        {
            var Q0;
            Q0=makeQuery(id+"F0.imprint","IMPRINT",FACE,{"disambiguationData":[TD([[makeQuery(id+"F0.imprint","IMPRINT",EDGE,{"derivedFrom":sQuery(id+"F0.wireOp",EDGE,"E6")}),-1.0]])]});
            var Q1;
            Q1=makeQuery(id+"F0.imprint","IMPRINT",FACE,{"disambiguationData":[TD([[makeQuery(id+"F0.imprint","IMPRINT",EDGE,{"derivedFrom":sQuery(id+"F0.wireOp",EDGE,"E45")}),1.0]])]});
            var Q2;
            Q2=makeQuery(id+"F0.imprint","IMPRINT",FACE,{"disambiguationData":[TD([[makeQuery(id+"F0.imprint","IMPRINT",EDGE,{"derivedFrom":sQuery(id+"F0.wireOp",EDGE,"E0")}),-1.0]])]});
            var Q3;
            Q3=makeQuery(id+"F0.imprint","IMPRINT",FACE,{"disambiguationData":[TD([[makeQuery(id+"F0.imprint","IMPRINT",EDGE,{"derivedFrom":sQuery(id+"F0.wireOp",EDGE,"E9")}),-1.0]])]});
            var Q4;
            Q4=makeQuery(id+"F0.imprint","IMPRINT",FACE,{"disambiguationData":[TD([[makeQuery(id+"F0.imprint","IMPRINT",EDGE,{"derivedFrom":sQuery(id+"F0.wireOp",EDGE,"E49")}),-1.0]])]});
            var Q5;
            Q5=makeQuery(id+"F0.imprint","IMPRINT",FACE,{"disambiguationData":[TD([[makeQuery(id+"F0.imprint","IMPRINT",EDGE,{"derivedFrom":sQuery(id+"F0.wireOp",EDGE,"E46")}),-1.0]])]});
            var Q6;
            {var subQ12=sQuery(id+"F0.wireOp",EDGE,"E43");Q6=makeQuery(id+"F0.imprint","IMPRINT",FACE,{"disambiguationData":[TD([[makeQuery(id+"F0.imprint","IMPRINT",EDGE,{"derivedFrom":subQ12}),1.0]])]});}
            var Q7;
            {var subQ0=sQuery(id+"F0.wireOp",EDGE,"E64");Q7=makeQuery(id+"F0.imprint","IMPRINT",FACE,{"disambiguationData":[TD([[makeQuery(id+"F0.imprint","IMPRINT",EDGE,{"derivedFrom":subQ0}),-1.0]])]});}
            var Q8;
            {var subQ0=sQuery(id+"F0.wireOp",EDGE,"E58");var subQ1=sQuery(id+"F0.wireOp",EDGE,"E57");var subQ2=makeQuery(id+"F0.imprint","INTERSECT",VERTEX,{"derivedFrom":[subQ1,subQ0]});Q8=makeQuery(id+"F0.imprint","IMPRINT",FACE,{"disambiguationData":[TD([[makeQuery(id+"F0.imprint","IMPRINT",EDGE,{"disambiguationData":[TD([[subQ2,1.0]])],"derivedFrom":subQ1}),-1.0]])]});}
            var Q9;
            {var subQ0=sQuery(id+"F0.wireOp",EDGE,"E200");Q9=makeQuery(id+"F0.imprint","IMPRINT",FACE,{"disambiguationData":[TD([[makeQuery(id+"F0.imprint","IMPRINT",EDGE,{"derivedFrom":subQ0}),-1.0]])]});}
            var Q10;
            {var subQ0=sQuery(id+"F0.wireOp",EDGE,"E99");Q10=makeQuery(id+"F0.imprint","IMPRINT",FACE,{"disambiguationData":[TD([[makeQuery(id+"F0.imprint","IMPRINT",EDGE,{"derivedFrom":subQ0}),-1.0]])]});}
            var Q11;
            {var subQ1=sQuery(id+"F0.wireOp",EDGE,"E44");var subQ3=sQuery(id+"F0.wireOp",EDGE,"E238.bottom");var subQ4=makeQuery(id+"F0.imprint","INTERSECT",VERTEX,{"derivedFrom":[subQ1,subQ3]});Q11=makeQuery(id+"F0.imprint","IMPRINT",FACE,{"disambiguationData":[TD([[makeQuery(id+"F0.imprint","IMPRINT",EDGE,{"disambiguationData":[TD([[subQ4,-1.0]])],"derivedFrom":subQ3}),1.0]])]});}
            var Q12;
            {var subQ0=sQuery(id+"F0.wireOp",EDGE,"E43");Q12=makeQuery(id+"F0.imprint","IMPRINT",FACE,{"disambiguationData":[TD([[makeQuery(id+"F0.imprint","IMPRINT",EDGE,{"derivedFrom":subQ0}),-1.0]])]});}
            var Q13;
            {var subQ3=sQuery(id+"F0.wireOp",EDGE,"E63");var subQ7=sQuery(id+"F0.wireOp",EDGE,"E238.top");var subQ9=makeQuery(id+"F0.imprint","INTERSECT",VERTEX,{"derivedFrom":[subQ3,subQ7]});Q13=makeQuery(id+"F0.imprint","IMPRINT",FACE,{"disambiguationData":[TD([[makeQuery(id+"F0.imprint","IMPRINT",EDGE,{"disambiguationData":[TD([[subQ9,1.0]])],"derivedFrom":subQ3}),-1.0]])]});}
            var Q14;
            {var subQ0=sQuery(id+"F0.wireOp",EDGE,"E238.top");var subQ1=sQuery(id+"F0.wireOp",EDGE,"E58");var subQ2=makeQuery(id+"F0.imprint","INTERSECT",VERTEX,{"derivedFrom":[subQ1,subQ0]});Q14=makeQuery(id+"F0.imprint","IMPRINT",FACE,{"disambiguationData":[TD([[makeQuery(id+"F0.imprint","IMPRINT",EDGE,{"disambiguationData":[TD([[subQ2,-1.0]])],"derivedFrom":subQ1}),1.0]])]});}
            var Q15;
            {var subQ0=sQuery(id+"F0.wireOp",EDGE,"E238.top");var subQ1=sQuery(id+"F0.wireOp",EDGE,"E57");var subQ2=makeQuery(id+"F0.imprint","INTERSECT",VERTEX,{"derivedFrom":[subQ1,subQ0]});Q15=makeQuery(id+"F0.imprint","IMPRINT",FACE,{"disambiguationData":[TD([[makeQuery(id+"F0.imprint","IMPRINT",EDGE,{"disambiguationData":[TD([[subQ2,1.0]])],"derivedFrom":subQ1}),-1.0]])]});}
            var Q16;
            {var subQ0=sQuery(id+"F0.wireOp",EDGE,"E238.top");var subQ1=sQuery(id+"F0.wireOp",EDGE,"E52");var subQ2=makeQuery(id+"F0.imprint","INTERSECT",VERTEX,{"derivedFrom":[subQ1,subQ0]});Q16=makeQuery(id+"F0.imprint","IMPRINT",FACE,{"disambiguationData":[TD([[makeQuery(id+"F0.imprint","IMPRINT",EDGE,{"disambiguationData":[TD([[subQ2,-1.0]])],"derivedFrom":subQ1}),1.0]])]});}
            var Q17;
            {var subQ5=sQuery(id+"F0.wireOp",EDGE,"E52");var subQ7=sQuery(id+"F0.wireOp",EDGE,"E238.top");var subQ8=makeQuery(id+"F0.imprint","INTERSECT",VERTEX,{"derivedFrom":[subQ5,subQ7]});Q17=makeQuery(id+"F0.imprint","IMPRINT",FACE,{"disambiguationData":[TD([[makeQuery(id+"F0.imprint","IMPRINT",EDGE,{"disambiguationData":[TD([[subQ8,-1.0]])],"derivedFrom":subQ5}),-1.0]])]});}
            var Q18;
            {var subQ0=sQuery(id+"F0.wireOp",EDGE,"E82");var subQ1=sQuery(id+"F0.wireOp",EDGE,"E52");var subQ2=makeQuery(id+"F0.imprint","INTERSECT",VERTEX,{"derivedFrom":[subQ1,subQ0]});Q18=makeQuery(id+"F0.imprint","IMPRINT",FACE,{"disambiguationData":[TD([[makeQuery(id+"F0.imprint","IMPRINT",EDGE,{"disambiguationData":[TD([[subQ2,-1.0]])],"derivedFrom":subQ1}),-1.0]])]});}
            var Q19;
            {var subQ20=sQuery(id+"F0.wireOp",EDGE,"E238.right");Q19=makeQuery(id+"F0.imprint","IMPRINT",FACE,{"disambiguationData":[TD([[makeQuery(id+"F0.imprint","IMPRINT",EDGE,{"derivedFrom":subQ20}),-1.0]])]});}
            var Q20;
            {var subQ0=sQuery(id+"F0.wireOp",EDGE,"E171");var subQ1=sQuery(id+"F0.wireOp",EDGE,"E100");var subQ2=makeQuery(id+"F0.imprint","INTERSECT",VERTEX,{"derivedFrom":[subQ1,subQ0]});Q20=makeQuery(id+"F0.imprint","IMPRINT",FACE,{"disambiguationData":[TD([[makeQuery(id+"F0.imprint","IMPRINT",EDGE,{"disambiguationData":[TD([[subQ2,-1.0]])],"derivedFrom":subQ1}),-1.0]])]});}
            var Q21;
            {var subQ0=sQuery(id+"F0.wireOp",EDGE,"E162");var subQ1=sQuery(id+"F0.wireOp",EDGE,"E161");var subQ2=makeQuery(id+"F0.imprint","INTERSECT",VERTEX,{"derivedFrom":[subQ1,subQ0]});Q21=makeQuery(id+"F0.imprint","IMPRINT",FACE,{"disambiguationData":[TD([[makeQuery(id+"F0.imprint","IMPRINT",EDGE,{"disambiguationData":[TD([[subQ2,1.0]])],"derivedFrom":subQ1}),-1.0]])]});}
            var Q22;
            {var subQ0=sQuery(id+"F0.wireOp",EDGE,"E238.bottom");var subQ1=sQuery(id+"F0.wireOp",EDGE,"E230");var subQ2=makeQuery(id+"F0.imprint","INTERSECT",VERTEX,{"disambiguationData":[OD(0.0)],"derivedFrom":[subQ1,subQ0]});Q22=makeQuery(id+"F0.imprint","IMPRINT",FACE,{"disambiguationData":[TD([[makeQuery(id+"F0.imprint","IMPRINT",EDGE,{"disambiguationData":[TD([[subQ2,-1.0]])],"derivedFrom":subQ1}),-1.0]])]});}
            var Q23;
            Q23=makeQuery(id+"F0.imprint","IMPRINT",FACE,{"disambiguationData":[TD([[makeQuery(id+"F0.imprint","IMPRINT",EDGE,{"derivedFrom":sQuery(id+"F0.wireOp",EDGE,"E240.bottom")}),1.0]])]});
            extrude(context, id + "F1", {"entities" : qUnion([Q0, Q1, Q2, Q3, Q4, Q5, Q6, Q7, Q8, Q9, Q10, Q11, Q12, Q13, Q14, Q15, Q16, Q17, Q18, Q19, Q20, Q21, Q22, Q23]), "depth" : 1.52 * mm, "offsetDistance" : 25.4 * mm});
        }
    });
